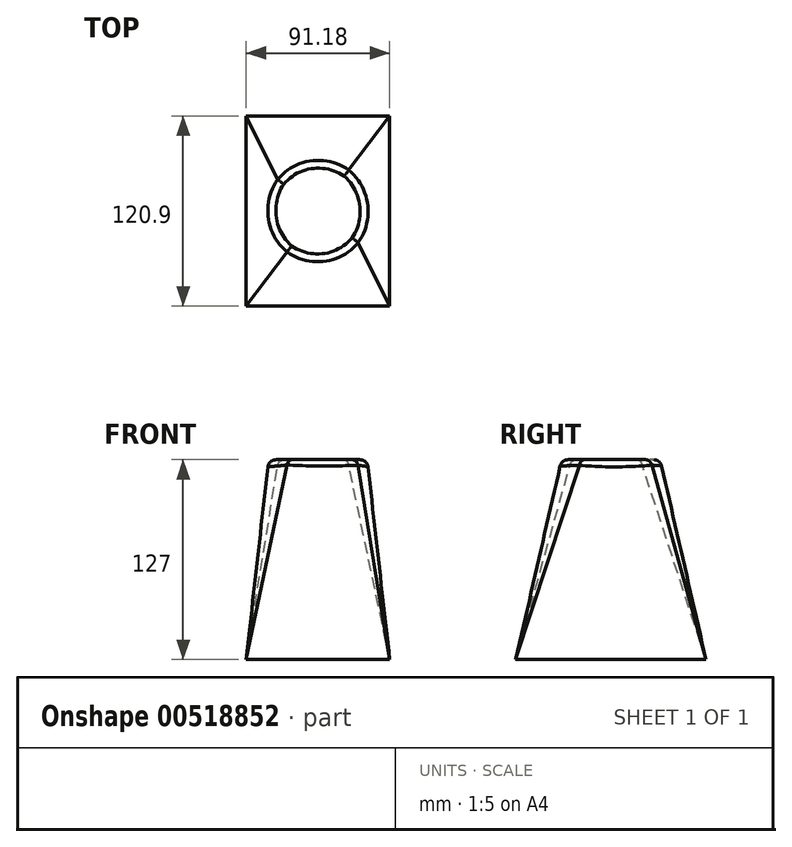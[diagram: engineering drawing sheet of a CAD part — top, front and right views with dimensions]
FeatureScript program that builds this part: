
annotation { "Feature Type Name" : "Feature", "Feature Type Description" : "" }
export const myFeature = defineFeature(function(context is Context, id is Id, definition is map)
    precondition{}
    {
        {
            var Q0;
            Q0=qCreatedBy(makeId("Top.planeOp"),FACE);
            var sketch = newSketch(context, id + "F0", { "sketchPlane" : qUnion([Q0])});
            skLineSegment(sketch, "E0.bottom", {"start": v(45.59, 60.45) * mm, "end": v(-45.59, 60.45) * mm});
            skLineSegment(sketch, "E0.top", {"start": v(45.59, -60.45) * mm, "end": v(-45.59, -60.45) * mm});
            skLineSegment(sketch, "E0.left", {"start": v(45.59, 60.45) * mm, "end": v(45.59, -60.45) * mm});
            skLineSegment(sketch, "E0.right", {"start": v(-45.59, 60.45) * mm, "end": v(-45.59, -60.45) * mm});
            skPoint(sketch, "E0.middle", {"position": v(0, 0) * mm});
            skSolve(sketch);
        }
        {
            var Q0;
            Q0=qCreatedBy(makeId("Top.planeOp"),FACE);
            cPlane(context, id + "F1", {"entities" : qUnion([Q0]), "cplaneType" : CPlaneType.OFFSET, "offset" : 127 * mm, "width" : 152.4 * mm, "height" : 152.4 * mm});
        }
        {
            var Q0;
            Q0=qCreatedBy(id+"F1.planeOp",FACE);
            var sketch = newSketch(context, id + "F2", { "sketchPlane" : qUnion([Q0])});
            skPoint(sketch, "E1.middle", {"position": v(0, 0) * mm});
            skCircle(sketch, "E2", {"center": v(0, 0) * mm, "radius": 31.3 * mm});
            skSolve(sketch);
        }
        {
            var Q0;
            Q0=makeQuery(id+"F0.imprint","IMPRINT",FACE,{"disambiguationData":[TD([[makeQuery(id+"F0.imprint","IMPRINT",EDGE,{"derivedFrom":sQuery(id+"F0.wireOp",EDGE,"E0.bottom")}),1.0]])]});
            var Q1;
            Q1=makeQuery(id+"F2.imprint","IMPRINT",FACE,{"disambiguationData":[TD([[makeQuery(id+"F2.imprint","IMPRINT",EDGE,{"derivedFrom":sQuery(id+"F2.wireOp",EDGE,"E2")}),1.0]])]});
            var Q2;
            Q2=makeQuery(id+"F2.imprint","IMPRINT",FACE,{"disambiguationData":[TD([[makeQuery(id+"F2.imprint","IMPRINT",EDGE,{"derivedFrom":sQuery(id+"F2.wireOp",EDGE,"E2")}),1.0]])]});
            var Q3;
            Q3=makeQuery(id+"F0.imprint","IMPRINT",FACE,{"disambiguationData":[TD([[makeQuery(id+"F0.imprint","IMPRINT",EDGE,{"derivedFrom":sQuery(id+"F0.wireOp",EDGE,"E0.bottom")}),1.0]])]});
            loft(context, id + "F3", {"sheetProfilesArray" : [{ "sheetProfileEntities" : qUnion([Q0]) }, { "sheetProfileEntities" : qUnion([Q1]) }], "wireProfilesArray" : [{ "wireProfileEntities" : qUnion([Q2]) }, { "wireProfileEntities" : qUnion([Q3]) }]});
        }
        {
            var Q0;
            Q0=makeQuery(id+"F3.opLoft","CAP_FACE",FACE,{"disambiguationData":[OSD([makeQuery(id+"F2.imprint","IMPRINT",FACE,{"disambiguationData":[TD([[makeQuery(id+"F2.imprint","IMPRINT",EDGE,{"derivedFrom":sQuery(id+"F2.wireOp",EDGE,"E2")}),1.0]])]})])],"isStart":true});
            fillet(context, id + "F4", {"entities" : qUnion([Q0]), "radius" : 5.08 * mm, "tangentPropagation" : true, "allowEdgeOverflow" : false});
        }
    });
